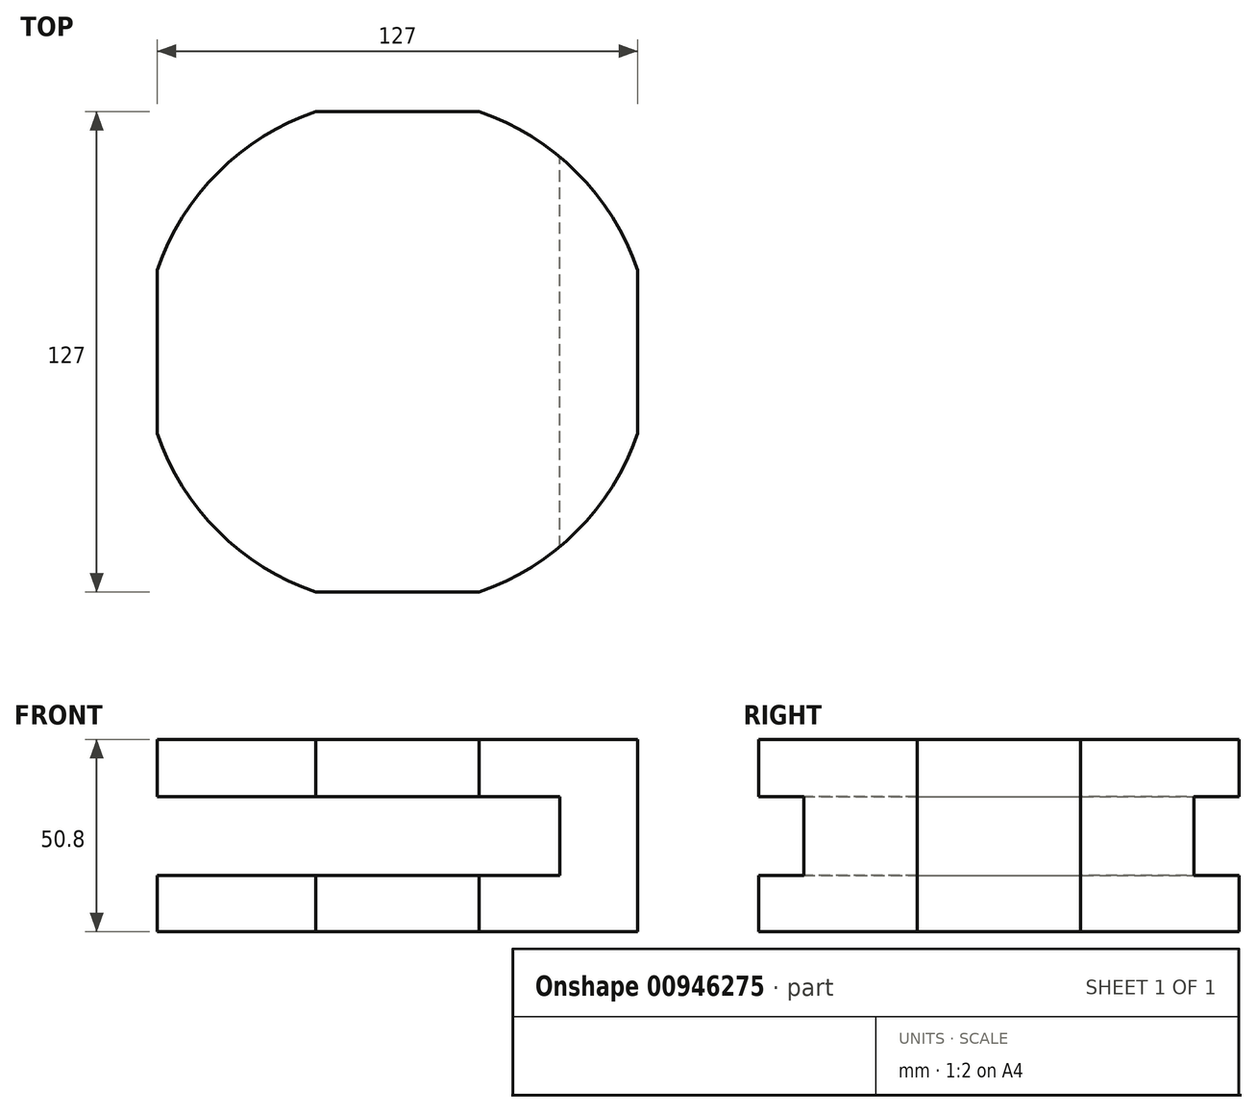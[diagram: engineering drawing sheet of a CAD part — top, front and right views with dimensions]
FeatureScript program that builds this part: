
annotation { "Feature Type Name" : "Feature", "Feature Type Description" : "" }
export const myFeature = defineFeature(function(context is Context, id is Id, definition is map)
    precondition{}
    {
        {
            var Q0;
            Q0=qCreatedBy(makeId("Top.planeOp"),FACE);
            var sketch = newSketch(context, id + "F0", { "sketchPlane" : qUnion([Q0])});
            skCircle(sketch, "E0", {"center": v(0, 0) * mm, "radius": 67.07 * mm});
            skLineSegment(sketch, "E1.bottom", {"start": v(63.5, -63.5) * mm, "end": v(-63.5, -63.5) * mm});
            skLineSegment(sketch, "E1.top", {"start": v(63.5, 63.5) * mm, "end": v(-63.5, 63.5) * mm});
            skLineSegment(sketch, "E1.left", {"start": v(63.5, -63.5) * mm, "end": v(63.5, 63.5) * mm});
            skLineSegment(sketch, "E1.right", {"start": v(-63.5, -63.5) * mm, "end": v(-63.5, 63.5) * mm});
            skSolve(sketch);
        }
        {
            var Q0;
            {var subQ1=sQuery(id+"F0.wireOp",EDGE,"E0");var subQ9=sQuery(id+"F0.wireOp",EDGE,"E1.top");var subQ12=makeQuery(id+"F0.imprint","INTERSECT",VERTEX,{"disambiguationData":[OD(0.0)],"derivedFrom":[subQ1,subQ9]});Q0=makeQuery(id+"F0.imprint","IMPRINT",FACE,{"disambiguationData":[TD([[makeQuery(id+"F0.imprint","IMPRINT",EDGE,{"disambiguationData":[TD([[subQ12,1.0]])],"derivedFrom":subQ1}),1.0]])]});}
            extrude(context, id + "F1", {"entities" : qUnion([Q0]), "depth" : 50.8 * mm, "offsetDistance" : 25.4 * mm});
        }
        {
            var Q0;
            Q0=qCreatedBy(makeId("Front.planeOp"),FACE);
            var sketch = newSketch(context, id + "F2", { "sketchPlane" : qUnion([Q0])});
            skLineSegment(sketch, "E2.bottom", {"start": v(-63.62, 35.64) * mm, "end": v(42.86, 35.64) * mm});
            skLineSegment(sketch, "E2.top", {"start": v(-63.62, 14.89) * mm, "end": v(42.86, 14.89) * mm});
            skLineSegment(sketch, "E2.left", {"start": v(-63.62, 35.64) * mm, "end": v(-63.62, 14.89) * mm});
            skLineSegment(sketch, "E2.right", {"start": v(42.86, 35.64) * mm, "end": v(42.86, 14.89) * mm});
            skSolve(sketch);
        }
        {
            var Q0;
            Q0 = qSketchRegion(id + "F2", true);
            extrude(context, id + "F3", {"entities" : qUnion([Q0]), "operationType" : NewBodyOperationType.REMOVE, "endBound" : BoundingType.SYMMETRIC, "depth" : 171.7 * mm, "offsetDistance" : 25.4 * mm});
        }
    });
